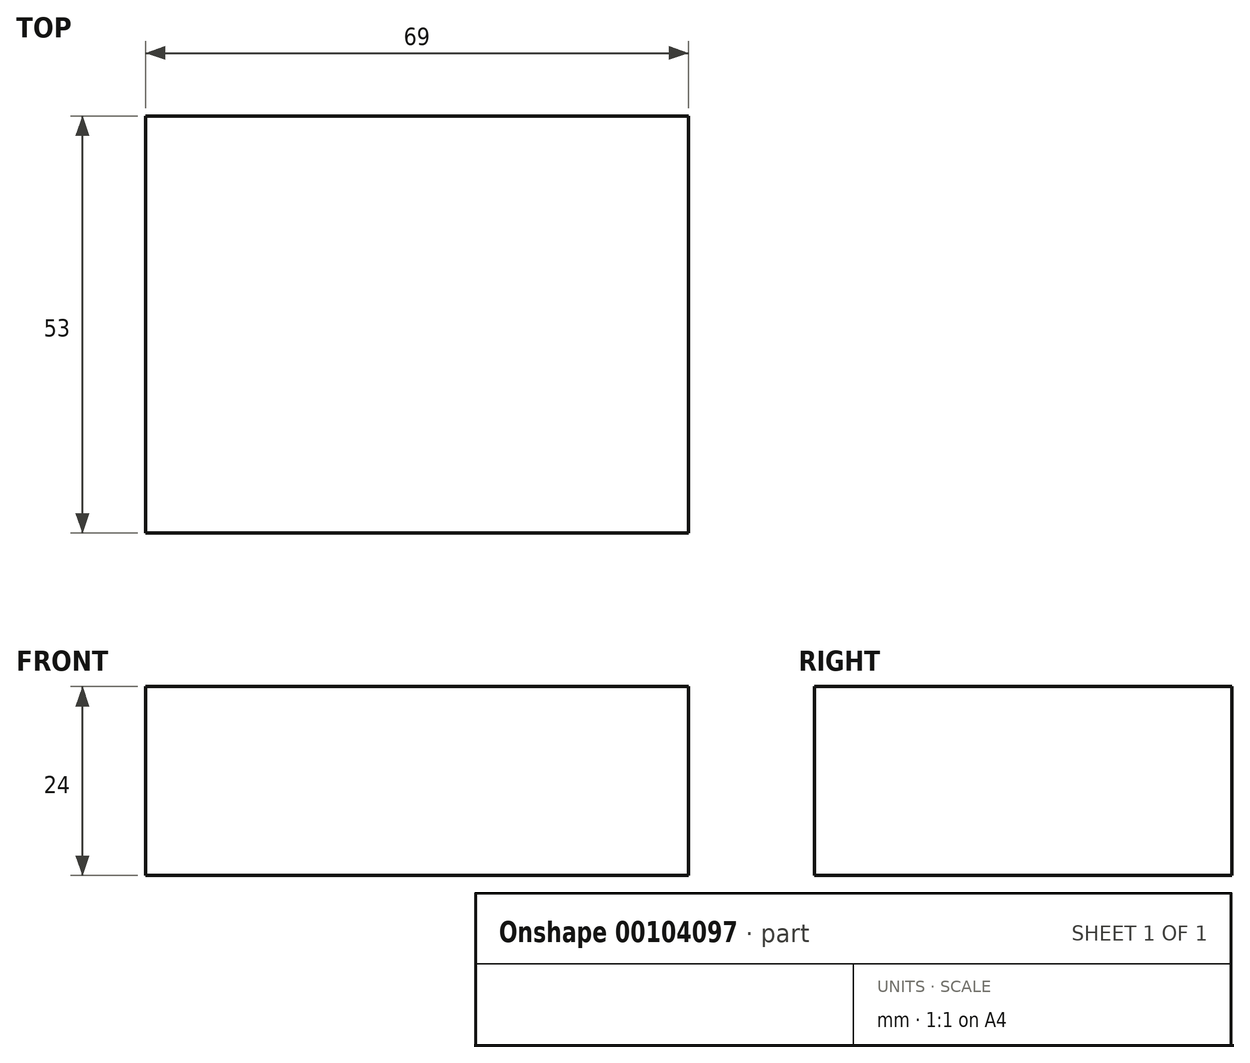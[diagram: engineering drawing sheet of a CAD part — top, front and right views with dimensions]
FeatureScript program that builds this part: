
annotation { "Feature Type Name" : "Feature", "Feature Type Description" : "" }
export const myFeature = defineFeature(function(context is Context, id is Id, definition is map)
    precondition{}
    {
        {
            var Q0;
            Q0=qCreatedBy(makeId("Front.planeOp"),FACE);
            var sketch = newSketch(context, id + "F0", { "sketchPlane" : qUnion([Q0])});
            skLineSegment(sketch, "E0.bottom", {"start": v(-26.58, 8.82) * mm, "end": v(42.42, 8.82) * mm});
            skLineSegment(sketch, "E0.top", {"start": v(-26.58, -15.18) * mm, "end": v(42.42, -15.18) * mm});
            skLineSegment(sketch, "E0.left", {"start": v(-26.58, 8.82) * mm, "end": v(-26.58, -15.18) * mm});
            skLineSegment(sketch, "E0.right", {"start": v(42.42, 8.82) * mm, "end": v(42.42, -15.18) * mm});
            skSolve(sketch);
        }
        {
            var Q0;
            Q0=makeQuery(id+"F0.imprint","IMPRINT",FACE,{"disambiguationData":[TD([[makeQuery(id+"F0.imprint","IMPRINT",EDGE,{"derivedFrom":sQuery(id+"F0.wireOp",EDGE,"E0.bottom")}),-1.0]])]});
            extrude(context, id + "F1", {"entities" : qUnion([Q0]), "depth" : 53 * mm});
        }
    });
